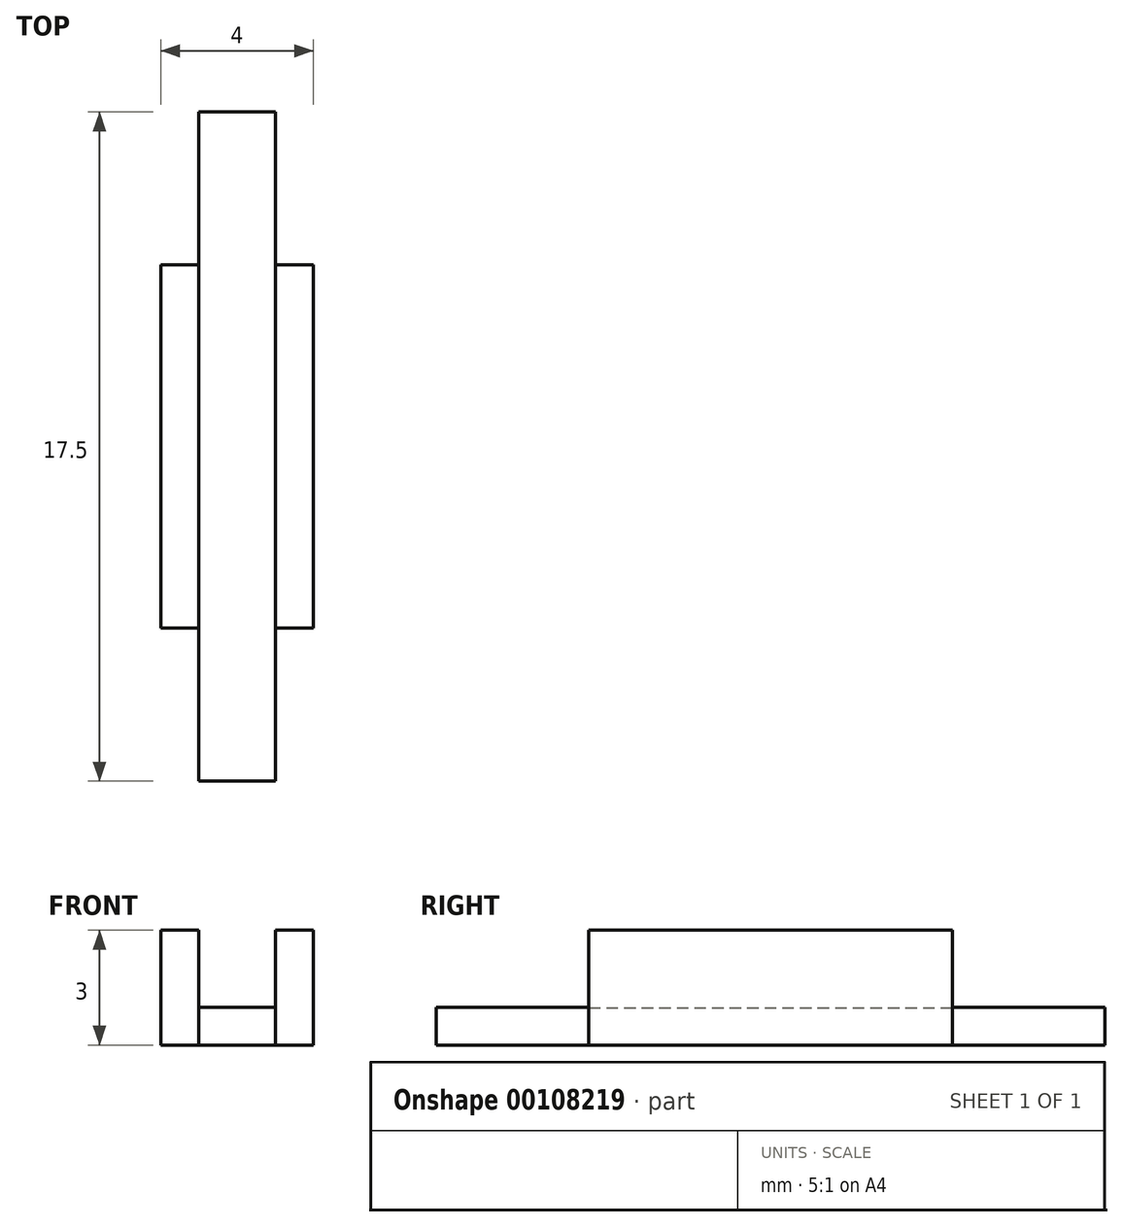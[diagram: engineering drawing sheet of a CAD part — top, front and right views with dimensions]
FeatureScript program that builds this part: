
annotation { "Feature Type Name" : "Feature", "Feature Type Description" : "" }
export const myFeature = defineFeature(function(context is Context, id is Id, definition is map)
    precondition{}
    {
        {
            var Q0;
            Q0=qCreatedBy(makeId("Front.planeOp"),FACE);
            var sketch = newSketch(context, id + "F0", { "sketchPlane" : qUnion([Q0])});
            skLineSegment(sketch, "E0.bottom", {"start": v(1, 0.49) * mm, "end": v(-1, 0.49) * mm});
            skLineSegment(sketch, "E0.top", {"start": v(1, -0.49) * mm, "end": v(-1, -0.49) * mm});
            skLineSegment(sketch, "E0.left", {"start": v(1, 0.49) * mm, "end": v(1, -0.49) * mm});
            skLineSegment(sketch, "E0.right", {"start": v(-1, 0.49) * mm, "end": v(-1, -0.49) * mm});
            skPoint(sketch, "E0.middle", {"position": v(0, 0) * mm});
            skLineSegment(sketch, "E1.bottom", {"start": v(1, -0.49) * mm, "end": v(2, -0.49) * mm});
            skLineSegment(sketch, "E1.top", {"start": v(1, 2.51) * mm, "end": v(2, 2.51) * mm});
            skLineSegment(sketch, "E1.left", {"start": v(1, -0.49) * mm, "end": v(1, 2.51) * mm});
            skLineSegment(sketch, "E1.right", {"start": v(2, -0.49) * mm, "end": v(2, 2.51) * mm});
            skLineSegment(sketch, "E2.bottom", {"start": v(-1, -0.49) * mm, "end": v(-2, -0.49) * mm});
            skLineSegment(sketch, "E2.top", {"start": v(-1, 2.51) * mm, "end": v(-2, 2.51) * mm});
            skLineSegment(sketch, "E2.left", {"start": v(-1, -0.49) * mm, "end": v(-1, 2.51) * mm});
            skLineSegment(sketch, "E2.right", {"start": v(-2, -0.49) * mm, "end": v(-2, 2.51) * mm});
            skSolve(sketch);
        }
        {
            var Q0;
            Q0 = qSketchRegion(id + "F0", true);
            extrude(context, id + "F1", {"entities" : qUnion([Q0]), "endBound" : BoundingType.SYMMETRIC, "depth" : 9.5 * mm});
        }
        {
            var Q0;
            Q0=qCreatedBy(makeId("Front.planeOp"),FACE);
            var sketch = newSketch(context, id + "F2", { "sketchPlane" : qUnion([Q0])});
            skLineSegment(sketch, "E3.bottom", {"start": v(-1, 0.5) * mm, "end": v(1, 0.5) * mm});
            skLineSegment(sketch, "E3.top", {"start": v(-1, -0.5) * mm, "end": v(1, -0.5) * mm});
            skLineSegment(sketch, "E3.left", {"start": v(-1, 0.5) * mm, "end": v(-1, -0.5) * mm});
            skLineSegment(sketch, "E3.right", {"start": v(1, 0.5) * mm, "end": v(1, -0.5) * mm});
            skSolve(sketch);
        }
        {
            var Q0;
            Q0 = qSketchRegion(id + "F2", true);
            extrude(context, id + "F3", {"entities" : qUnion([Q0]), "operationType" : NewBodyOperationType.ADD, "endBound" : BoundingType.SYMMETRIC, "depth" : 13.5 * mm});
        }
        {
            var Q0;
            Q0=makeQuery(id+"F3.opExtrude","CAP_FACE",FACE,{"disambiguationData":[OSD([sQuery(id+"F2.wireOp",EDGE,"E3.bottom"),sQuery(id+"F2.wireOp",EDGE,"E3.top"),sQuery(id+"F2.wireOp",EDGE,"E3.left"),sQuery(id+"F2.wireOp",EDGE,"E3.right")])],"isStart":false});
            var Q1;
            Q1=makeQuery(id+"F3.opExtrude","CAP_FACE",FACE,{"disambiguationData":[OSD([sQuery(id+"F2.wireOp",EDGE,"E3.bottom"),sQuery(id+"F2.wireOp",EDGE,"E3.top"),sQuery(id+"F2.wireOp",EDGE,"E3.left"),sQuery(id+"F2.wireOp",EDGE,"E3.right")])],"isStart":true});
            extrude(context, id + "F4", {"entities" : qUnion([Q0, Q1]), "operationType" : NewBodyOperationType.ADD, "depth" : 2 * mm});
        }
        {
            var Q0;
            Q0=makeQuery(id+"F3.opExtrude","CAP_FACE",FACE,{"disambiguationData":[OSD([sQuery(id+"F2.wireOp",EDGE,"E3.bottom"),sQuery(id+"F2.wireOp",EDGE,"E3.top"),sQuery(id+"F2.wireOp",EDGE,"E3.left"),sQuery(id+"F2.wireOp",EDGE,"E3.right")])],"isStart":true});
            extrude(context, id + "F5", {"entities" : qUnion([Q0]), "operationType" : NewBodyOperationType.ADD, "depth" : 2 * mm});
        }
    });
